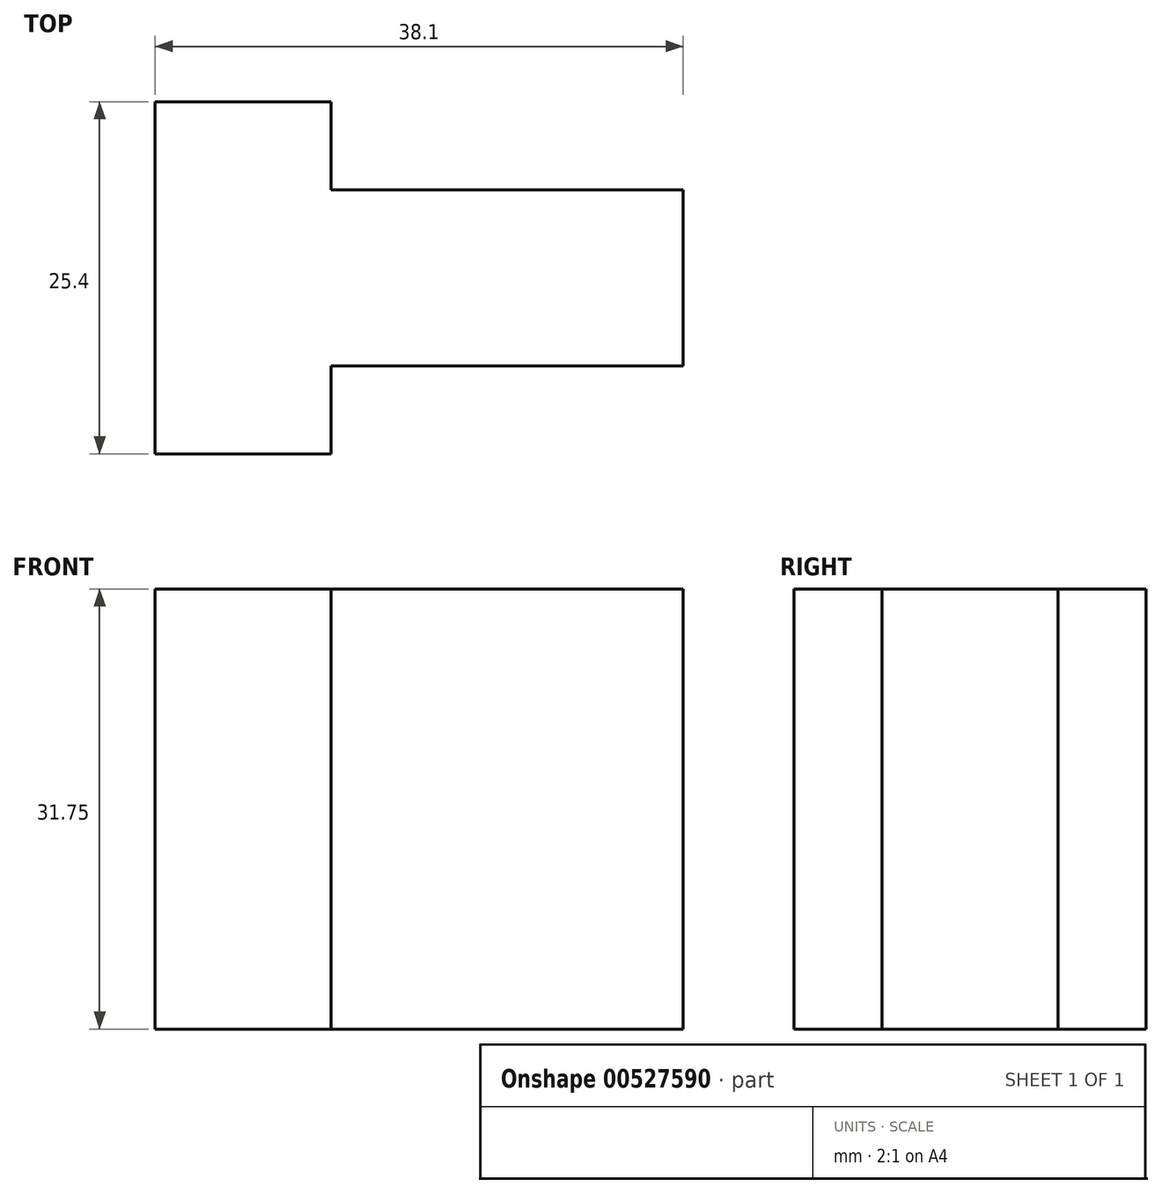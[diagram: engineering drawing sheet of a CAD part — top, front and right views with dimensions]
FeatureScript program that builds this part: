
annotation { "Feature Type Name" : "Feature", "Feature Type Description" : "" }
export const myFeature = defineFeature(function(context is Context, id is Id, definition is map)
    precondition{}
    {
        {
            var Q0;
            Q0=qCreatedBy(makeId("Top.planeOp"),FACE);
            var sketch = newSketch(context, id + "F0", { "sketchPlane" : qUnion([Q0])});
            skLineSegment(sketch, "E0", {"start": v(0, 0) * mm, "end": v(0, 25.4) * mm});
            skLineSegment(sketch, "E1", {"start": v(0, 0) * mm, "end": v(12.7, 0) * mm});
            skLineSegment(sketch, "E2", {"start": v(12.7, 0) * mm, "end": v(12.7, 6.35) * mm});
            skLineSegment(sketch, "E3", {"start": v(12.7, 6.35) * mm, "end": v(38.1, 6.35) * mm});
            skLineSegment(sketch, "E4", {"start": v(38.1, 6.35) * mm, "end": v(38.1, 19.05) * mm});
            skLineSegment(sketch, "E5", {"start": v(38.1, 19.05) * mm, "end": v(12.7, 19.05) * mm});
            skLineSegment(sketch, "E6", {"start": v(12.7, 19.05) * mm, "end": v(12.7, 25.4) * mm});
            skLineSegment(sketch, "E7", {"start": v(0, 25.4) * mm, "end": v(12.7, 25.4) * mm});
            skSolve(sketch);
        }
        {
            var Q0;
            Q0=makeQuery(id+"F0.imprint","IMPRINT",FACE,{"disambiguationData":[TD([[makeQuery(id+"F0.imprint","IMPRINT",EDGE,{"derivedFrom":sQuery(id+"F0.wireOp",EDGE,"E0")}),-1.0]])]});
            extrude(context, id + "F1", {"entities" : qUnion([Q0]), "depth" : 31.75 * mm, "offsetDistance" : 25.4 * mm});
        }
    });
